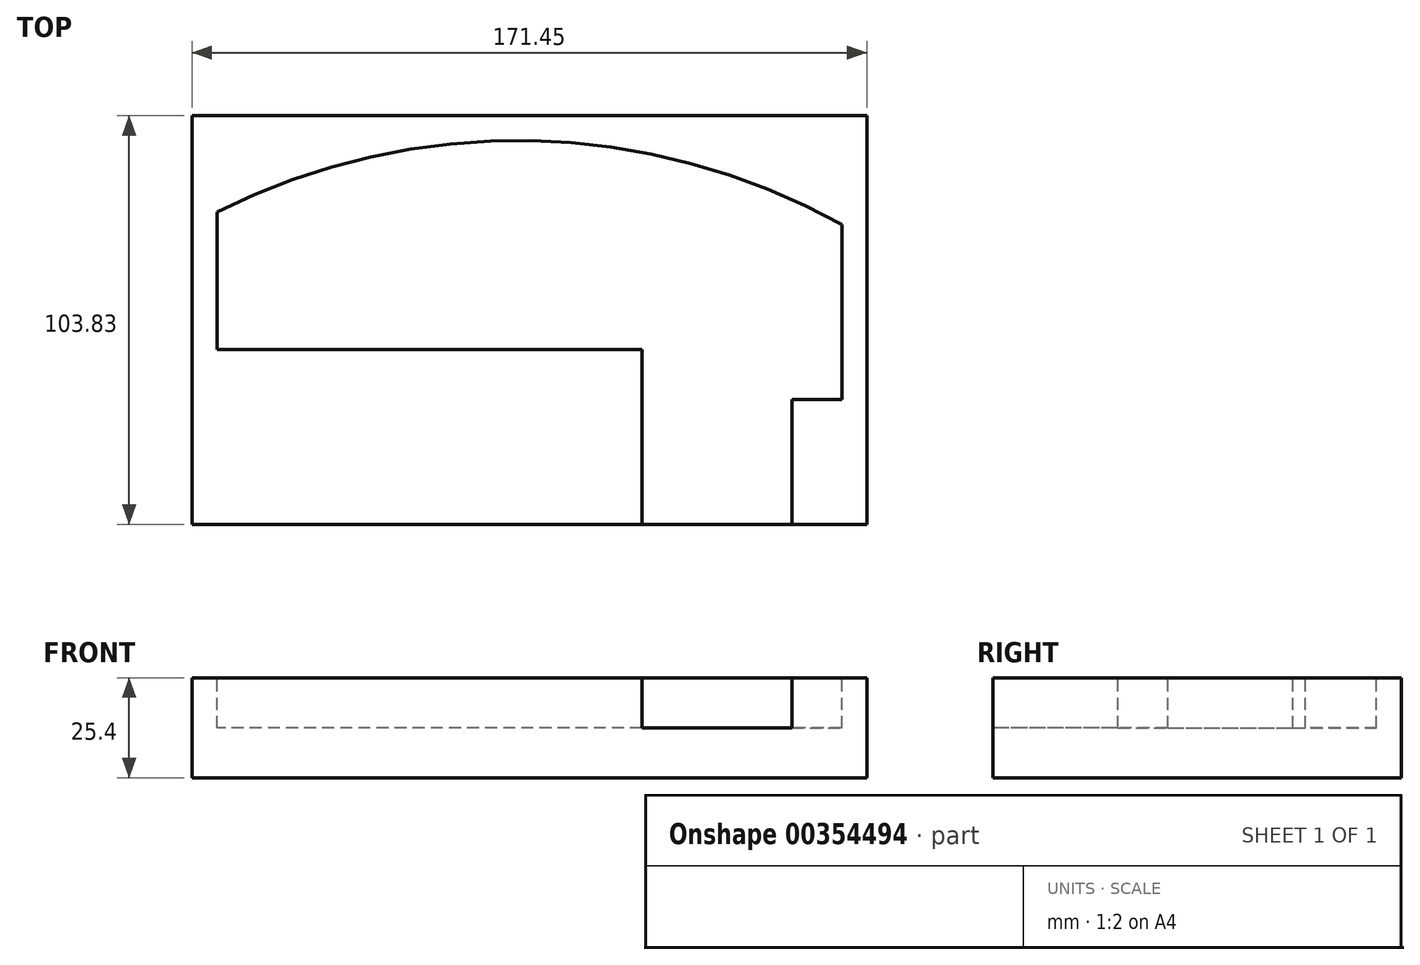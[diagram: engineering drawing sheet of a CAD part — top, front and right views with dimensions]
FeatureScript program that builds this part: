
annotation { "Feature Type Name" : "Feature", "Feature Type Description" : "" }
export const myFeature = defineFeature(function(context is Context, id is Id, definition is map)
    precondition{}
    {
        {
            var Q0;
            Q0=qCreatedBy(makeId("Top.planeOp"),FACE);
            var sketch = newSketch(context, id + "F0", { "sketchPlane" : qUnion([Q0])});
            skLineSegment(sketch, "E0.MirrorCS", {"start": v(65.9, -29.08) * mm, "end": v(78.6, -29.08) * mm});
            skLineSegment(sketch, "E1.MirrorCS", {"start": v(78.6, -29.08) * mm, "end": v(78.6, 15.37) * mm});
            skLineSegment(sketch, "E2.MirrorCS", {"start": v(27.8, -16.38) * mm, "end": v(-80.15, -16.38) * mm});
            skLineSegment(sketch, "E3.MirrorCS", {"start": v(-80.15, -16.38) * mm, "end": v(-80.15, 18.54) * mm});
            skArc(sketch, "E4.MirrorCS", {"start": v(-80.15, 18.54) * mm, "mid": v(-0.38, 36.61) * mm, "end": v(78.6, 15.37) * mm});
            skLineSegment(sketch, "E5.MirrorCS", {"start": v(65.9, -54.48) * mm, "end": v(27.8, -54.48) * mm});
            skLineSegment(sketch, "E6.MirrorCS", {"start": v(65.9, -29.08) * mm, "end": v(65.9, -54.48) * mm});
            skLineSegment(sketch, "E7.MirrorCS", {"start": v(27.8, -16.38) * mm, "end": v(27.8, -54.48) * mm});
            skSolve(sketch);
        }
        {
            var Q0;
            Q0 = qSketchRegion(id + "F0", true);
            extrude(context, id + "F1", {"entities" : qUnion([Q0]), "depth" : 12.7 * mm});
        }
        {
            var Q0;
            Q0=makeQuery(id+"F1.opExtrude","CAP_FACE",FACE,{"disambiguationData":[OSD([sQuery(id+"F0.wireOp",EDGE,"E0.MirrorCS"),sQuery(id+"F0.wireOp",EDGE,"E1.MirrorCS"),sQuery(id+"F0.wireOp",EDGE,"E2.MirrorCS"),sQuery(id+"F0.wireOp",EDGE,"E3.MirrorCS"),sQuery(id+"F0.wireOp",EDGE,"E4.MirrorCS"),sQuery(id+"F0.wireOp",EDGE,"E5.MirrorCS"),sQuery(id+"F0.wireOp",EDGE,"E6.MirrorCS"),sQuery(id+"F0.wireOp",EDGE,"E7.MirrorCS")])],"isStart":true});
            var sketch = newSketch(context, id + "F2", { "sketchPlane" : qUnion([Q0])});
            skLineSegment(sketch, "E8.bottom", {"start": v(84.95, 60.83) * mm, "end": v(-86.5, 60.83) * mm});
            skLineSegment(sketch, "E8.top", {"start": v(84.95, -43) * mm, "end": v(-86.5, -43) * mm});
            skLineSegment(sketch, "E8.left", {"start": v(84.95, 60.83) * mm, "end": v(84.95, -43) * mm});
            skLineSegment(sketch, "E8.right", {"start": v(-86.5, 60.83) * mm, "end": v(-86.5, -43) * mm});
            skSolve(sketch);
        }
        {
            var Q0;
            Q0 = qSketchRegion(id + "F2", true);
            extrude(context, id + "F3", {"entities" : qUnion([Q0]), "operationType" : NewBodyOperationType.ADD, "depth" : 25.4 * mm});
        }
        {
            var Q0;
            Q0=makeQuery(id+"F1.opExtrude","CAP_FACE",FACE,{"disambiguationData":[OSD([sQuery(id+"F0.wireOp",EDGE,"E0.MirrorCS"),sQuery(id+"F0.wireOp",EDGE,"E1.MirrorCS"),sQuery(id+"F0.wireOp",EDGE,"E2.MirrorCS"),sQuery(id+"F0.wireOp",EDGE,"E3.MirrorCS"),sQuery(id+"F0.wireOp",EDGE,"E4.MirrorCS"),sQuery(id+"F0.wireOp",EDGE,"E5.MirrorCS"),sQuery(id+"F0.wireOp",EDGE,"E6.MirrorCS"),sQuery(id+"F0.wireOp",EDGE,"E7.MirrorCS")])],"isStart":false});
            extrude(context, id + "F4", {"entities" : qUnion([Q0]), "operationType" : NewBodyOperationType.REMOVE, "oppositeDirection" : true, "depth" : 25.4 * mm});
        }
        {
            var Q0;
            Q0=makeQuery(id+"F3.opExtrude","CAP_FACE",FACE,{"disambiguationData":[OSD([sQuery(id+"F2.wireOp",EDGE,"E8.bottom"),sQuery(id+"F2.wireOp",EDGE,"E8.top"),sQuery(id+"F2.wireOp",EDGE,"E8.left"),sQuery(id+"F2.wireOp",EDGE,"E8.right")])],"isStart":true});
            var sketch = newSketch(context, id + "F5", { "sketchPlane" : qUnion([Q0])});
            skLineSegment(sketch, "E9", {"start": v(27.8, -54.48) * mm, "end": v(27.8, -60.83) * mm});
            skLineSegment(sketch, "E10", {"start": v(65.9, -54.48) * mm, "end": v(65.9, -60.83) * mm});
            skLineSegment(sketch, "E11", {"start": v(27.8, -60.83) * mm, "end": v(65.9, -60.83) * mm});
            skLineSegment(sketch, "E12", {"start": v(65.9, -54.48) * mm, "end": v(27.8, -54.48) * mm});
            skSolve(sketch);
        }
        {
            var Q0;
            Q0 = qSketchRegion(id + "F5", true);
            extrude(context, id + "F6", {"entities" : qUnion([Q0]), "operationType" : NewBodyOperationType.REMOVE, "oppositeDirection" : true, "depth" : 12.7 * mm});
        }
    });
